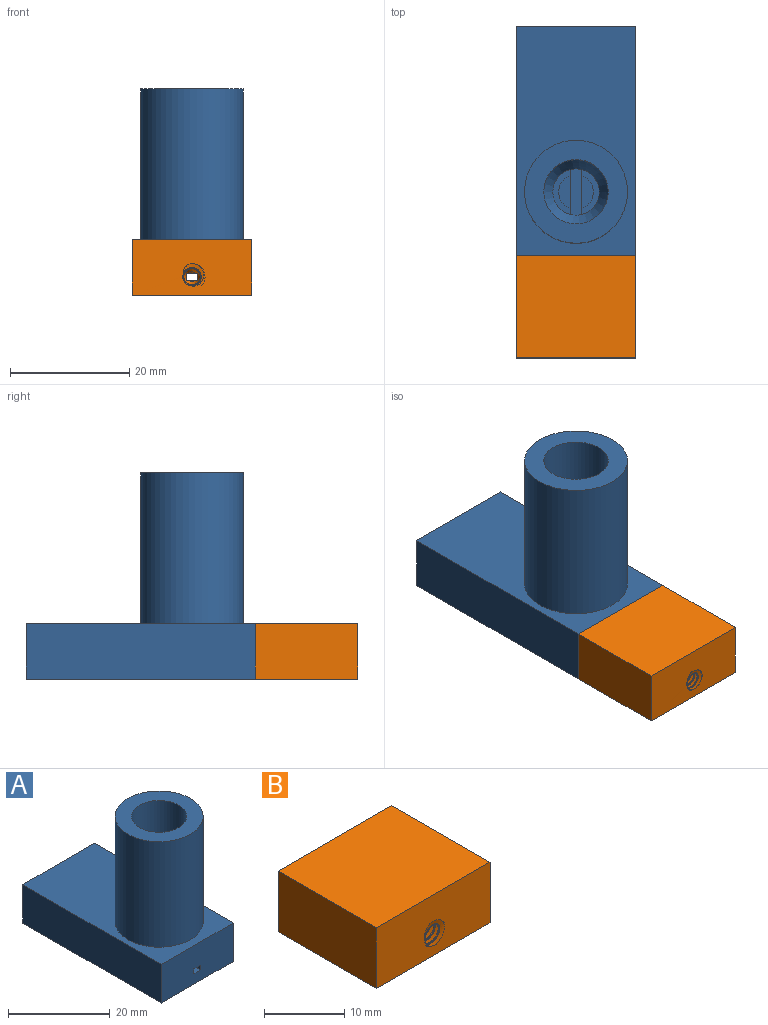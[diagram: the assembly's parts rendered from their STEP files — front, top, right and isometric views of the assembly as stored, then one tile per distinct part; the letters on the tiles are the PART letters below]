
ASSEMBLY  parts=2 mates=1
PART A: 39 faces, bbox 21.1x39.9x35.7 mm
  f0: plane 5.47x1.95mm, normal (0,0,1), area 7.8mm2, adj f3,f36
  f1: cone r=0.81mm half-angle=23.8deg, axis (0,1,0), area 0mm2, adj f2,f32
  f2: cone r=1.38mm half-angle=20.6deg, axis (0,1,0), area 9.6mm2, adj f1,f7,f23,f32,f33,f34,f36
  f3: cylinder r=2.9mm len=5.47mm, axis (0,0,1), area 8mm2, adj f0,f36,f38
  f4: plane 20x9.25mm, normal (0,-1,0), area 182.8mm2, adj f5,f14,f15,f16,f32,f33,f35,f36
  f5: plane 38.48x20mm, normal (0,0,-1), area 769.5mm2, adj f4,f14,f16,f17
  f6: plane 5.47x1.95mm, normal (0,0,1), area 7.8mm2, adj f8,f33
  f7: cone r=0.81mm half-angle=23.8deg, axis (0,1,0), area 0mm2, adj f2,f34
  f8: cylinder r=2.9mm len=5.47mm, axis (0,0,1), area 8mm2, adj f6,f33,f37
  f9: cylinder r=5.41mm len=26.91mm, axis (0,0,1), area 914.7mm2, adj f10,f13
  f10: cone r=5.41mm half-angle=27.5deg, axis (0,0,1), area 95.7mm2, adj f9,f11
  f11: cylinder r=3.9mm len=7.79mm, axis (0,0,1), area 22mm2, adj f10,f33,f34,f35,f36,f37,f38
  f12: cylinder r=8.65mm len=25.36mm, axis (0,0,-1), area 1378.1mm2, adj f13,f15
  f13: plane 17.3x17.3mm, normal (0,0,1), area 143mm2, adj f9,f12
  f14: plane 38.48x9.25mm, normal (-1,0,0), area 355.9mm2, adj f4,f5,f15,f17
  f15: plane 38.48x20mm, normal (0,0,1), area 534.5mm2, adj f4,f12,f14,f16,f17
  f16: plane 38.48x9.25mm, normal (1,0,0), area 355.9mm2, adj f4,f5,f15,f17
  f17: plane 20.33x9.58mm, normal (0,1,0), area 175mm2, adj f5,f14,f15,f16,f18,f24,f25,f26
  f18: cylinder r=1.38mm len=2.77mm, axis (0,1,0), area 0.6mm2, adj f17,f19,f30,f31
  f19: cylinder r=1.38mm len=2.77mm, axis (0,1,0), area 1mm2, adj f18,f20,f30,f31
  f20: cylinder r=1.38mm len=2.77mm, axis (0,1,0), area 1mm2, adj f19,f21,f30,f31
  f21: cylinder r=1.38mm len=2.77mm, axis (0,1,0), area 1mm2, adj f20,f22,f30,f31
  f22: cylinder r=1.38mm len=2.77mm, axis (0,1,0), area 1mm2, adj f21,f23,f30,f31
  f23: cylinder r=1.38mm len=2.77mm, axis (0,1,0), area 3.7mm2, adj f2,f22,f29,f31
  f24: bspline ~4.56x3.47mm, area 3.2mm2, adj f17,f25,f29,f31
  f25: bspline ~5x4.75mm, area 43.6mm2, adj f17,f24,f26,f29
  f26: bspline ~5x4.36mm, area 7mm2, adj f17,f25,f27,f29
  f27: bspline ~5x4.36mm, area 39.6mm2, adj f17,f26,f28,f29
  f28: bspline ~4.02x3.47mm, area 2.1mm2, adj f17,f27,f29,f30
  f29: plane 0.78x0.68mm, normal (0,0,1), area 0.3mm2, adj f23,f24,f25,f26,f27,f28,f30,f31
  f30: bspline ~3.84x3.47mm, area 5mm2, adj f17,f18,f19,f20,f21,f22,f28,f29
  f31: bspline ~4.51x3.47mm, area 6mm2, adj f17,f18,f19,f20,f21,f22,f23,f24
  f32: plane 34.42x2.98mm, normal (0,0,1), area 61.2mm2, adj f1,f2,f4,f33,f36
  f33: plane 33.53x1.66mm, normal (1,0,0), area 35mm2, adj f2,f4,f6,f8,f11,f32,f34,f35
  f34: plane 20.05x2.98mm, normal (0,0,-1), area 34mm2, adj f2,f7,f11,f33,f36
  f35: plane 6.81x1.89mm, normal (0,0,-1), area 12.7mm2, adj f4,f11,f33,f36
  f36: plane 33.32x1.46mm, normal (-1,0,0), area 35mm2, adj f0,f2,f3,f4,f11,f32,f34,f35
  f37: plane 7.56x2.95mm, normal (0,0,1), area 8.8mm2, adj f8,f11,f33
  f38: plane 7.56x2.95mm, normal (0,0,1), area 8.8mm2, adj f3,f11,f36
PART B: 22 faces, bbox 21.1x18.7x10.3 mm
  f0: cone r=1.38mm half-angle=20.6deg, axis (0,-1,0), area 9.7mm2, adj f1,f9,f17,f18,f19,f20,f21
  f1: cone r=0.81mm half-angle=23.8deg, axis (0,-1,0), area 0mm2, adj f0,f18
  f2: plane 20x9.25mm, normal (0,1,0), area 182.8mm2, adj f13,f14,f15,f16,f18,f19,f20,f21
  f3: plane 0.76x0.68mm, normal (0.35,0,0.94), area 0.3mm2, adj f4,f5,f6,f7,f8,f9,f10,f11
  f4: bspline ~5.06x4.55mm, area 42.7mm2, adj f3,f5,f11,f12
  f5: bspline ~5.06x4.48mm, area 8.4mm2, adj f3,f4,f6,f12
  f6: bspline ~5.06x4.63mm, area 42.4mm2, adj f3,f5,f7,f12
  f7: bspline ~4.53x3.55mm, area 1.6mm2, adj f3,f6,f8,f12
  f8: bspline ~4.41x3.07mm, area 7.9mm2, adj f3,f7,f9,f12
  f9: cylinder r=1.38mm len=4.41mm, axis (0,1,0), area 8.2mm2, adj f0,f3,f8,f10,f12
  f10: bspline ~3.84x3.55mm, area 6.6mm2, adj f3,f9,f11,f12
  f11: bspline ~4.04x3.55mm, area 3.5mm2, adj f3,f4,f10,f12
  f12: plane 20.41x9.66mm, normal (0,-1,0), area 174.6mm2, adj f4,f5,f6,f7,f8,f9,f10,f11
  f13: plane 17.28x9.25mm, normal (1,0,0), area 159.8mm2, adj f2,f12,f14,f16
  f14: plane 20x17.28mm, normal (0,0,1), area 345.6mm2, adj f2,f12,f13,f15
  f15: plane 17.28x9.25mm, normal (-1,0,0), area 159.8mm2, adj f2,f12,f14,f16
  f16: plane 20x17.28mm, normal (0,0,-1), area 345.6mm2, adj f2,f12,f13,f15
  f17: cone r=0.81mm half-angle=23.8deg, axis (0,-1,0), area 0mm2, adj f0,f20
  f18: plane 13.24x2.98mm, normal (0,0,1), area 21.3mm2, adj f0,f1,f2,f19,f21
  f19: plane 12.15x1.18mm, normal (1,0,0), area 14mm2, adj f0,f2,f18,f20
  f20: plane 13.24x2.98mm, normal (0,0,-1), area 21.3mm2, adj f0,f2,f17,f19,f21
  f21: plane 12.18x1.22mm, normal (-1,0,0), area 14mm2, adj f0,f2,f18,f20
PLACE A t=(-63.98,-5.77,7.69)mm
PLACE B t=(-63.98,0.73,7.69)mm
MATE fastened A.f4 <-> B.f2  axis (0,-1,0) through (-34.67,-5.97,9.51)mm
